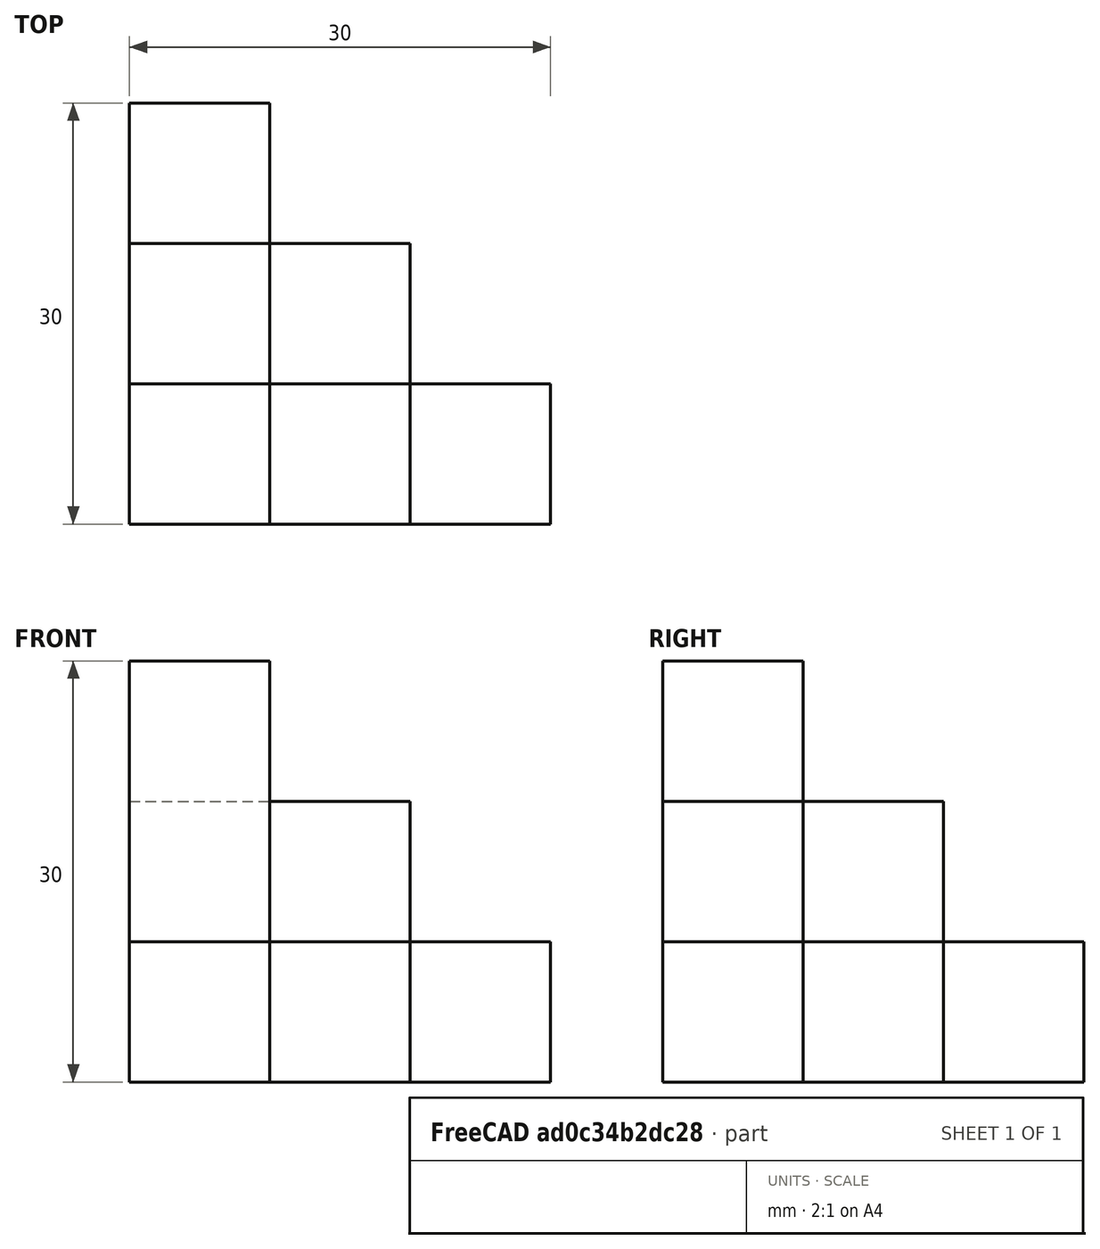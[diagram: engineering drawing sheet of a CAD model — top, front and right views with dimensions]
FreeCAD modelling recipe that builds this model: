
FCSTD DOCUMENT  (FreeCAD 1.0R39319 (Git))
Label: ojt1_t04r01_qcub_3nivells
License: All rights reserved
LicenseURL: https://en.wikipedia.org/wiki/All_rights_reserved
objects: Part::Box×7
note: 7 computed .brp shape members not serialized (recipe doc carries the construction recipe); baked Part::Feature solids carry a one-line shape summary decoded from their .brp

FEATURE [Part::Box] Box  label="Cub"
  AttacherType = Attacher::AttachEngine3D
  Height = 30
  Length = 10
  Width = 10
FEATURE [Part::Box] Box001  label="Cub001"
  AttacherType = Attacher::AttachEngine3D
  Height = 20
  Length = 10
  Placement = pos=(0,10,0) rot=(0,10,1;0rad)
  Width = 10
FEATURE [Part::Box] Box002  label="Cub002"
  AttacherType = Attacher::AttachEngine3D
  Height = 10
  Length = 10
  Placement = pos=(10,0,0) rot=(0,0,1;0rad)
  Width = 20
FEATURE [Part::Box] Box003  label="Cub003"
  AttacherType = Attacher::AttachEngine3D
  Height = 10
  Length = 10
  Placement = pos=(20,0,0) rot=(0,0,1;0rad)
  Width = 10
FEATURE [Part::Box] Box004  label="Cub004"
  AttacherType = Attacher::AttachEngine3D
  Height = 10
  Length = 10
  Placement = pos=(0,20,0) rot=(0,0,1;0rad)
  Width = 10
FEATURE [Part::Box] Box005  label="Cub005"
  AttacherType = Attacher::AttachEngine3D
  Height = 10
  Length = 10
  Width = 10
FEATURE [Part::Box] Box006  label="Cub006"
  AttacherType = Attacher::AttachEngine3D
  Height = 20
  Length = 10
  Placement = pos=(10,0,0) rot=(0,0,1;0rad)
  Width = 10
